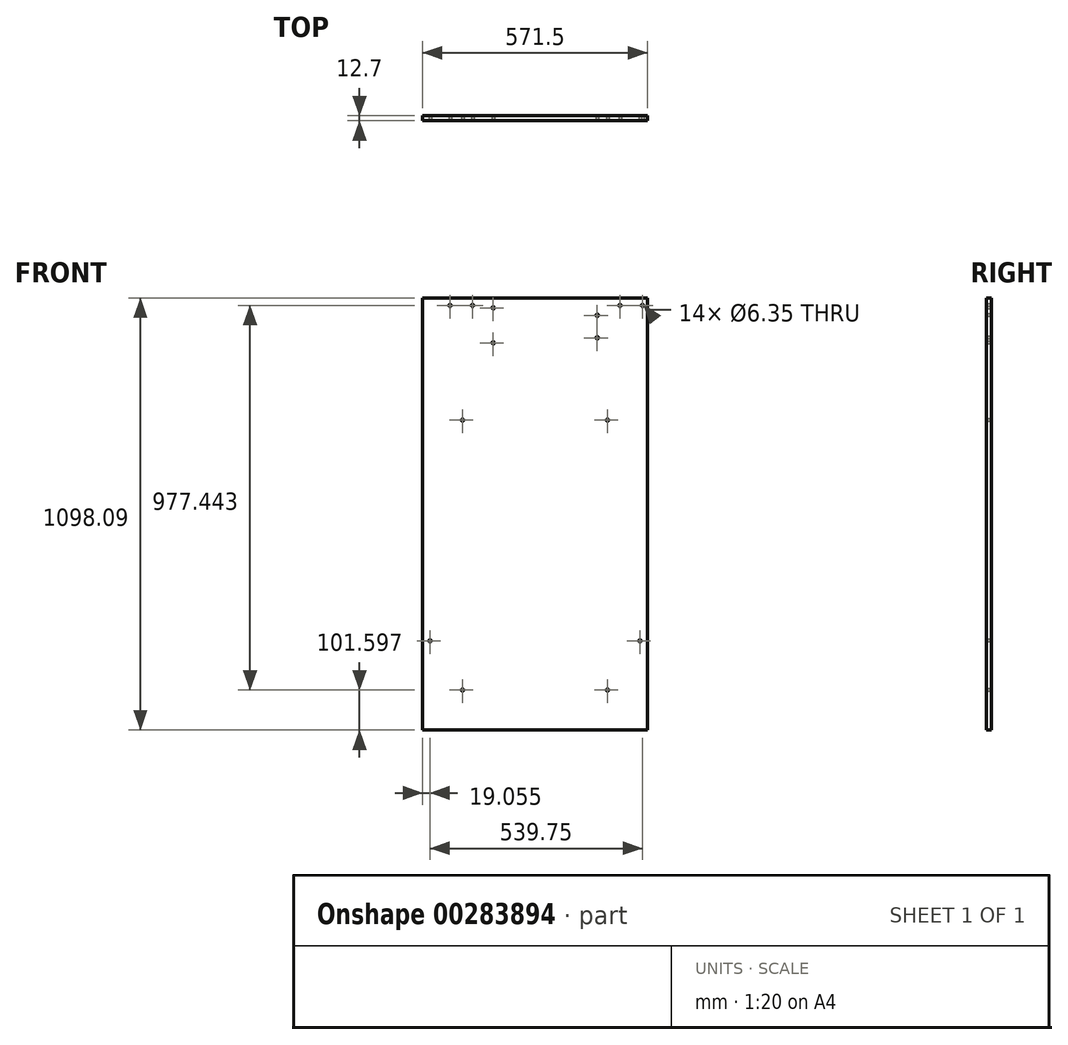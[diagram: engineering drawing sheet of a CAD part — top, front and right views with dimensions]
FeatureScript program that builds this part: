
annotation { "Feature Type Name" : "Feature", "Feature Type Description" : "" }
export const myFeature = defineFeature(function(context is Context, id is Id, definition is map)
    precondition{}
    {
        {
            var Q0;
            Q0=qCreatedBy(makeId("Front.planeOp"),FACE);
            var sketch = newSketch(context, id + "F0", { "sketchPlane" : qUnion([Q0])});
            skLineSegment(sketch, "E0.bottom", {"start": v(0, 0) * mm, "end": v(784.22, 0) * mm});
            skLineSegment(sketch, "E0.top", {"start": v(0, 508) * mm, "end": v(784.22, 508) * mm});
            skLineSegment(sketch, "E0.left", {"start": v(0, 0) * mm, "end": v(0, 508) * mm});
            skLineSegment(sketch, "E0.right", {"start": v(784.23, 0) * mm, "end": v(784.23, 508) * mm});
            skSolve(sketch);
        }
        {
            var Q0;
            Q0 = qSketchRegion(id + "F0", true);
            extrude(context, id + "F1", {"entities" : qUnion([Q0]), "depth" : 12.7 * mm});
        }
        {
            var Q0;
            Q0=makeQuery(id+"F1.opExtrude","CAP_FACE",FACE,{"disambiguationData":[OSD([sQuery(id+"F0.wireOp",EDGE,"E0.bottom"),sQuery(id+"F0.wireOp",EDGE,"E0.top"),sQuery(id+"F0.wireOp",EDGE,"E0.left"),sQuery(id+"F0.wireOp",EDGE,"E0.right")])],"isStart":false});
            var sketch = newSketch(context, id + "F2", { "sketchPlane" : qUnion([Q0])});
            skPoint(sketch, "E1", {"position": v(392.11, 482.6) * mm});
            skPoint(sketch, "E1.positionSnap0", {"position": v(392.11, 508) * mm});
            skPoint(sketch, "E2", {"position": v(392.11, 393.7) * mm});
            skSolve(sketch);
        }
        {
            var Q0;
            Q0=sQuery(id+"F2.wireOp",VERTEX,"E1");
            var Q1;
            Q1=sQuery(id+"F2.wireOp",VERTEX,"E2");
            var Q2;
            Q2=makeQuery(id+"F1.opExtrude","SWEPT_BODY",BODY,{"disambiguationData":[OSD([sQuery(id+"F0.wireOp",EDGE,"E0.bottom"),sQuery(id+"F0.wireOp",EDGE,"E0.top"),sQuery(id+"F0.wireOp",EDGE,"E0.left"),sQuery(id+"F0.wireOp",EDGE,"E0.right")])]});
            hole(context, id + "F3", {"style" : HoleStyle.SIMPLE, "endStyle" : HoleEndStyle.THROUGH, "holeDiameter" : 6.35 * mm, "tappedDepth" : 12.7 * mm, "tapClearance" : 3, "locations" : qUnion([Q0, Q1]), "scope" : qUnion([Q2])});
        }
        {
            var Q0;
            Q0=makeQuery(id+"F1.opExtrude","CAP_FACE",FACE,{"disambiguationData":[OSD([sQuery(id+"F0.wireOp",EDGE,"E0.bottom"),sQuery(id+"F0.wireOp",EDGE,"E0.top"),sQuery(id+"F0.wireOp",EDGE,"E0.left"),sQuery(id+"F0.wireOp",EDGE,"E0.right")])],"isStart":false});
            var sketch = newSketch(context, id + "F4", { "sketchPlane" : qUnion([Q0])});
            skPoint(sketch, "E3", {"position": v(771.52, 488.95) * mm});
            skPoint(sketch, "E4", {"position": v(714.38, 488.95) * mm});
            skPoint(sketch, "E5", {"position": v(339.72, 488.95) * mm});
            skPoint(sketch, "E6", {"position": v(282.57, 488.95) * mm});
            skSolve(sketch);
        }
        {
            var Q0;
            Q0=sQuery(id+"F4.wireOp",VERTEX,"E3");
            var Q1;
            Q1=sQuery(id+"F4.wireOp",VERTEX,"E4");
            var Q2;
            Q2=sQuery(id+"F4.wireOp",VERTEX,"E5");
            var Q3;
            Q3=sQuery(id+"F4.wireOp",VERTEX,"E6");
            var Q4;
            Q4=makeQuery(id+"F1.opExtrude","SWEPT_BODY",BODY,{"disambiguationData":[OSD([sQuery(id+"F0.wireOp",EDGE,"E0.bottom"),sQuery(id+"F0.wireOp",EDGE,"E0.top"),sQuery(id+"F0.wireOp",EDGE,"E0.left"),sQuery(id+"F0.wireOp",EDGE,"E0.right")])]});
            hole(context, id + "F5", {"style" : HoleStyle.SIMPLE, "endStyle" : HoleEndStyle.THROUGH, "holeDiameter" : 6.35 * mm, "tappedDepth" : 12.7 * mm, "tapClearance" : 3, "locations" : qUnion([Q0, Q1, Q2, Q3]), "scope" : qUnion([Q4])});
        }
        {
            var Q0;
            Q0=makeQuery(id+"F1.opExtrude","SWEPT_FACE",FACE,{"disambiguationData":[OSD([sQuery(id+"F0.wireOp",EDGE,"E0.left")])]});
            extrude(context, id + "F6", {"entities" : qUnion([Q0]), "operationType" : NewBodyOperationType.REMOVE, "oppositeDirection" : true, "depth" : 212.72 * mm});
        }
        {
            var Q0;
            Q0=makeQuery(id+"F1.opExtrude","CAP_FACE",FACE,{"disambiguationData":[OSD([sQuery(id+"F0.wireOp",EDGE,"E0.bottom"),sQuery(id+"F0.wireOp",EDGE,"E0.top"),sQuery(id+"F0.wireOp",EDGE,"E0.left"),sQuery(id+"F0.wireOp",EDGE,"E0.right")])],"isStart":false});
            var sketch = newSketch(context, id + "F7", { "sketchPlane" : qUnion([Q0])});
            skPoint(sketch, "E7", {"position": v(656.54, 463.55) * mm});
            skPoint(sketch, "E8", {"position": v(656.54, 406.4) * mm});
            skSolve(sketch);
        }
        {
            var Q0;
            Q0=sQuery(id+"F7.wireOp",VERTEX,"E7");
            var Q1;
            Q1=sQuery(id+"F7.wireOp",VERTEX,"E8");
            var Q2;
            Q2=makeQuery(id+"F1.opExtrude","SWEPT_BODY",BODY,{"disambiguationData":[OSD([sQuery(id+"F0.wireOp",EDGE,"E0.bottom"),sQuery(id+"F0.wireOp",EDGE,"E0.top"),sQuery(id+"F0.wireOp",EDGE,"E0.left"),sQuery(id+"F0.wireOp",EDGE,"E0.right")])]});
            hole(context, id + "F8", {"style" : HoleStyle.SIMPLE, "endStyle" : HoleEndStyle.THROUGH, "holeDiameter" : 6.35 * mm, "tappedDepth" : 12.7 * mm, "tapClearance" : 3, "locations" : qUnion([Q0, Q1]), "scope" : qUnion([Q2])});
        }
        {
            var Q0;
            Q0=makeQuery(id+"F1.opExtrude","SWEPT_FACE",FACE,{"disambiguationData":[OSD([sQuery(id+"F0.wireOp",EDGE,"E0.bottom")])]});
            extrude(context, id + "F9", {"entities" : qUnion([Q0]), "operationType" : NewBodyOperationType.ADD, "depth" : 590.1 * mm});
        }
        {
            var Q0;
            {var subQ0=sQuery(id+"F0.wireOp",EDGE,"E0.bottom");Q0=makeQuery(id+"F9.boolean.opBoolean","MERGE",FACE,{"derivedFrom":[makeQuery(id+"F1.opExtrude","CAP_FACE",FACE,{"disambiguationData":[OSD([subQ0,sQuery(id+"F0.wireOp",EDGE,"E0.top"),sQuery(id+"F0.wireOp",EDGE,"E0.left"),sQuery(id+"F0.wireOp",EDGE,"E0.right")])],"isStart":false}),makeQuery(id+"F9.opExtrude","SWEPT_FACE",FACE,{"disambiguationData":[OSD([subQ0]),TDD([makeQuery(id+"F1.opExtrude","CAP_EDGE",EDGE,{"disambiguationData":[OSD([subQ0])],"isStart":false})])]})]});}
            var sketch = newSketch(context, id + "F10", { "sketchPlane" : qUnion([Q0])});
            skLineSegment(sketch, "E9", {"start": v(498.48, 508) * mm, "end": v(498.48, -590.1) * mm, "construction": true});
            skPoint(sketch, "E10", {"position": v(231.78, -363.4) * mm});
            skPoint(sketch, "E11.MirrorP", {"position": v(765.18, -363.4) * mm});
            skSolve(sketch);
        }
        {
            var Q0;
            Q0=sQuery(id+"F10.wireOp",VERTEX,"E10");
            var Q1;
            Q1=sQuery(id+"F10.wireOp",VERTEX,"E11.MirrorP");
            var Q2;
            Q2=makeQuery(id+"F1.opExtrude","SWEPT_BODY",BODY,{"disambiguationData":[OSD([sQuery(id+"F0.wireOp",EDGE,"E0.bottom"),sQuery(id+"F0.wireOp",EDGE,"E0.top"),sQuery(id+"F0.wireOp",EDGE,"E0.left"),sQuery(id+"F0.wireOp",EDGE,"E0.right")])]});
            hole(context, id + "F11", {"style" : HoleStyle.SIMPLE, "endStyle" : HoleEndStyle.THROUGH, "holeDiameter" : 6.35 * mm, "tappedDepth" : 12.7 * mm, "tapClearance" : 3, "locations" : qUnion([Q0, Q1]), "scope" : qUnion([Q2])});
        }
        {
            var Q0;
            {var subQ0=sQuery(id+"F0.wireOp",EDGE,"E0.bottom");Q0=makeQuery(id+"F9.boolean.opBoolean","MERGE",FACE,{"derivedFrom":[makeQuery(id+"F1.opExtrude","CAP_FACE",FACE,{"disambiguationData":[OSD([subQ0,sQuery(id+"F0.wireOp",EDGE,"E0.top"),sQuery(id+"F0.wireOp",EDGE,"E0.left"),sQuery(id+"F0.wireOp",EDGE,"E0.right")])],"isStart":false}),makeQuery(id+"F9.opExtrude","SWEPT_FACE",FACE,{"disambiguationData":[OSD([subQ0]),TDD([makeQuery(id+"F1.opExtrude","CAP_EDGE",EDGE,{"disambiguationData":[OSD([subQ0])],"isStart":false})])]})]});}
            var sketch = newSketch(context, id + "F12", { "sketchPlane" : qUnion([Q0])});
            skPoint(sketch, "E12", {"position": v(682.63, -488.5) * mm});
            skPoint(sketch, "E13", {"position": v(682.62, 197.3) * mm});
            skLineSegment(sketch, "E14", {"start": v(498.48, 508) * mm, "end": v(498.48, -590.1) * mm, "construction": true});
            skPoint(sketch, "E15.MirrorP", {"position": v(314.33, 197.3) * mm});
            skPoint(sketch, "E16.MirrorP", {"position": v(314.33, -488.5) * mm});
            skSolve(sketch);
        }
        {
            var Q0;
            Q0=sQuery(id+"F12.wireOp",VERTEX,"E13");
            var Q1;
            Q1=sQuery(id+"F12.wireOp",VERTEX,"E15.MirrorP");
            var Q2;
            Q2=sQuery(id+"F12.wireOp",VERTEX,"E16.MirrorP");
            var Q3;
            Q3=sQuery(id+"F12.wireOp",VERTEX,"E12");
            var Q4;
            Q4=makeQuery(id+"F1.opExtrude","SWEPT_BODY",BODY,{"disambiguationData":[OSD([sQuery(id+"F0.wireOp",EDGE,"E0.bottom"),sQuery(id+"F0.wireOp",EDGE,"E0.top"),sQuery(id+"F0.wireOp",EDGE,"E0.left"),sQuery(id+"F0.wireOp",EDGE,"E0.right")])]});
            hole(context, id + "F13", {"style" : HoleStyle.SIMPLE, "endStyle" : HoleEndStyle.THROUGH, "holeDiameter" : 6.35 * mm, "tappedDepth" : 12.7 * mm, "tapClearance" : 3, "locations" : qUnion([Q0, Q1, Q2, Q3]), "scope" : qUnion([Q4])});
        }
    });
